# Revit family: Storage-Teknion-COSD_Overhead_Sliding_Door-R2021
name_source: partatom
category: Furniture
units: mm (PartAtom-declared; Revit-internal decimal feet)

## family parameters
Always vertical = Yes
Cut with Voids When Loaded = No
OmniClass Number = 23.40.20.00
OmniClass Title = General Furniture and Specialties
Room Calculation Point = No
Shared = Yes
Work Plane-Based = No

## types (3) — shared parameters
Assembly Code = E2020200
Manufacturer = Teknion
Manufacturer Fax = 416.661.4586
Part Number = COSD
Product Documentation Link = https://www.teknion.com
Product Line = Chronicle
Product Page URL = https://www.teknion.com
Series = Chronicle
Sustainability Data = https://www.teknion.com
URL = www.teknion.com
Unit Weight URL = http://www.teknion.com
Warranty = http://www.teknion.com
zero-valued in all types: Default Elevation

## per-type parameters (varying)
| type | 2H | Description | Distance | Flat Shelf Edge | Height | Knife Shelf Edge | Model |
| 1H | No | Chronicle Overhead, Sliding Door  , 1H Height | 5 " | No | 14.75 " | No | COSD1H15_ |
| 2H with Flat Visible Shelf Edge | Yes | Chronicle Overhead, Sliding Door  , 2H Height with Flat Visible Shelf Edge | 8 " | Yes | 28.5 " | No | COSD2H15_F |
| 2H with Knife Visible Shelf Edge | Yes | Chronicle Overhead, Sliding Door  , 2H Height with Knife Visible Shelf Edge | 8 " | No | 28.5 " | Yes | COSD2H15_K |

## geometry (parser evidence)
native form markers: Sweep x3
no freeform markers — native parametric forms only
